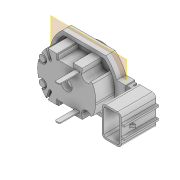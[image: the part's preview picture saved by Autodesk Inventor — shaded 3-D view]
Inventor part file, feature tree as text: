
AUTODESK INVENTOR PART (.ipt)
format: ipt  version: 2021 (Build 250183000, 183)  size: 464,896 bytes
history: native  units: in
note: dims shown in document units (in); Inventor stores cm internally (conversion verified against a paired STEP export)
features: extrude x20, sketch x20, projected_geometry x7, plane x1, chamfer x1
ambient origin geometry x8: Origin, YZ Plane, XZ Plane, XY Plane, X Axis, Y Axis, Z Axis, Center Point
bodies: Solid1 (feature_tree)
feature tree (49):
  extrude  "Extrusion1"  Depth=1.1969in
  extrude  "Extrusion2"  Depth=0.1969in TaperAngle=0.0deg
  plane  "Work Plane1"
  extrude  "Extrusion3"  Depth=0.1969in TaperAngle=0.0deg
  extrude  "Extrusion4"  Depth=0.0394in
  extrude  "Extrusion5"  Depth=0.0394in TaperAngle=0.0deg
  extrude  "Extrusion6"  Depth=0.3543in
  extrude  "Extrusion7"  Depth=0.1575in
  chamfer  "Chamfer1"  Distance=0.4331in
  extrude  "Extrusion8"  Depth=0.0984in
  extrude  "Extrusion9"  Depth=0.4331in TaperAngle=0.0deg
  extrude  "Extrusion10"  Depth=0.2559in
  extrude  "Extrusion11"  Depth=0.1969in
  extrude  "Extrusion12"  Depth=0.0197in
  extrude  "Extrusion13"  Depth=0.0787in
  extrude  "Extrusion14"  Depth=0.6299in TaperAngle=0.0deg
  extrude  "Extrusion15"  Depth=0.0787in
  extrude  "Extrusion16"  Depth=0.0787in TaperAngle=0.0deg
  extrude  "Extrusion17"  Depth=0.6496in
  extrude  "Extrusion18"  Depth=0.4134in
  extrude  "Extrusion19"  Depth=0.0787in
  extrude  "Extrusion20"  Depth=0.748in TaperAngle=0.0deg
  sketch  "Sketch1"  dims[d0=1.4961in d1=1.1969in]
  sketch  "Sketch2"  dims[d2=0.2756in d3=0.1969in d4=0.0in]
  projected_geometry  "Projected Loop1"
  sketch  "Sketch3"  dims[d5=0.0787in d6=0.1969in d7=0.0in]
  projected_geometry  "Projected Loop2"
  sketch  "Sketch4"  dims[d8=0.0394in d9=0.0in d10=0.8858in]
  sketch  "Sketch5"  dims[d11=0.2362in d12=0.0in d13=0.0394in d14=0.0in]
  projected_geometry  "Projected Loop3"
  sketch  "Sketch6"  dims[d15=0.0394in d16=0.3543in]
  projected_geometry  "Projected Loop4"
  sketch  "Sketch7"  dims[d17=0.2362in d18=0.1575in]
  sketch  "Sketch8"  dims[d19=0.2441in]
  sketch  "Sketch9"  dims[d20=0.2047in]
  projected_geometry  "Projected Loop5"
  sketch  "Sketch10"  dims[d21=0.0197in]
  projected_geometry  "Projected Loop6"
  sketch  "Sketch11"  dims[d24=0.0591in]
  sketch  "Sketch12"  dims[d27=0.1378in]
  sketch  "Sketch13"  dims[d28=0.1969in]
  projected_geometry  "Projected Loop7"
  sketch  "Sketch14"  dims[d29=0.1969in d30=0.4331in d31=0.0in]
  sketch  "Sketch15"  dims[d32=0.1181in d33=0.0984in]
  sketch  "Sketch16"  dims[d34=0.0197in d35=0.4331in d36=0.0in]
  sketch  "Sketch17"  dims[d37=0.0197in d38=0.0787in d39=45.0deg d40=0.2559in]
  sketch  "Sketch18"  dims[d41=0.2559in d42=0.1969in]
  sketch  "Sketch19"  dims[d43=0.1969in d44=0.0in d45=0.0197in]
  sketch  "Sketch20"  dims[d46=0.0591in d47=0.0in d48=0.0787in d49=0.6299in d50=0.0in d51=0.0787in d52=0.0787in d53=0.0in d55=0.6496in d56=0.4134in d57=0.0787in d58=0.748in d59=0.0in d60=0.0394in d61=0.6693in d62=0.0in d63=0.0591in d64=0.4724in d65=0.0in d66=0.0591in d67=0.0787in d68=0.0in d69=0.0394in d70=0.0591in d71=0.0in d73=0.0787in d74=0.0591in d75=0.0591in d76=0.0in d77=0.0591in d78=0.0in d79=0.0984in d80=0.0197in d81=0.002in d82=0.0787in d83=0.0in d84=0.0394in d85=0.0in]
